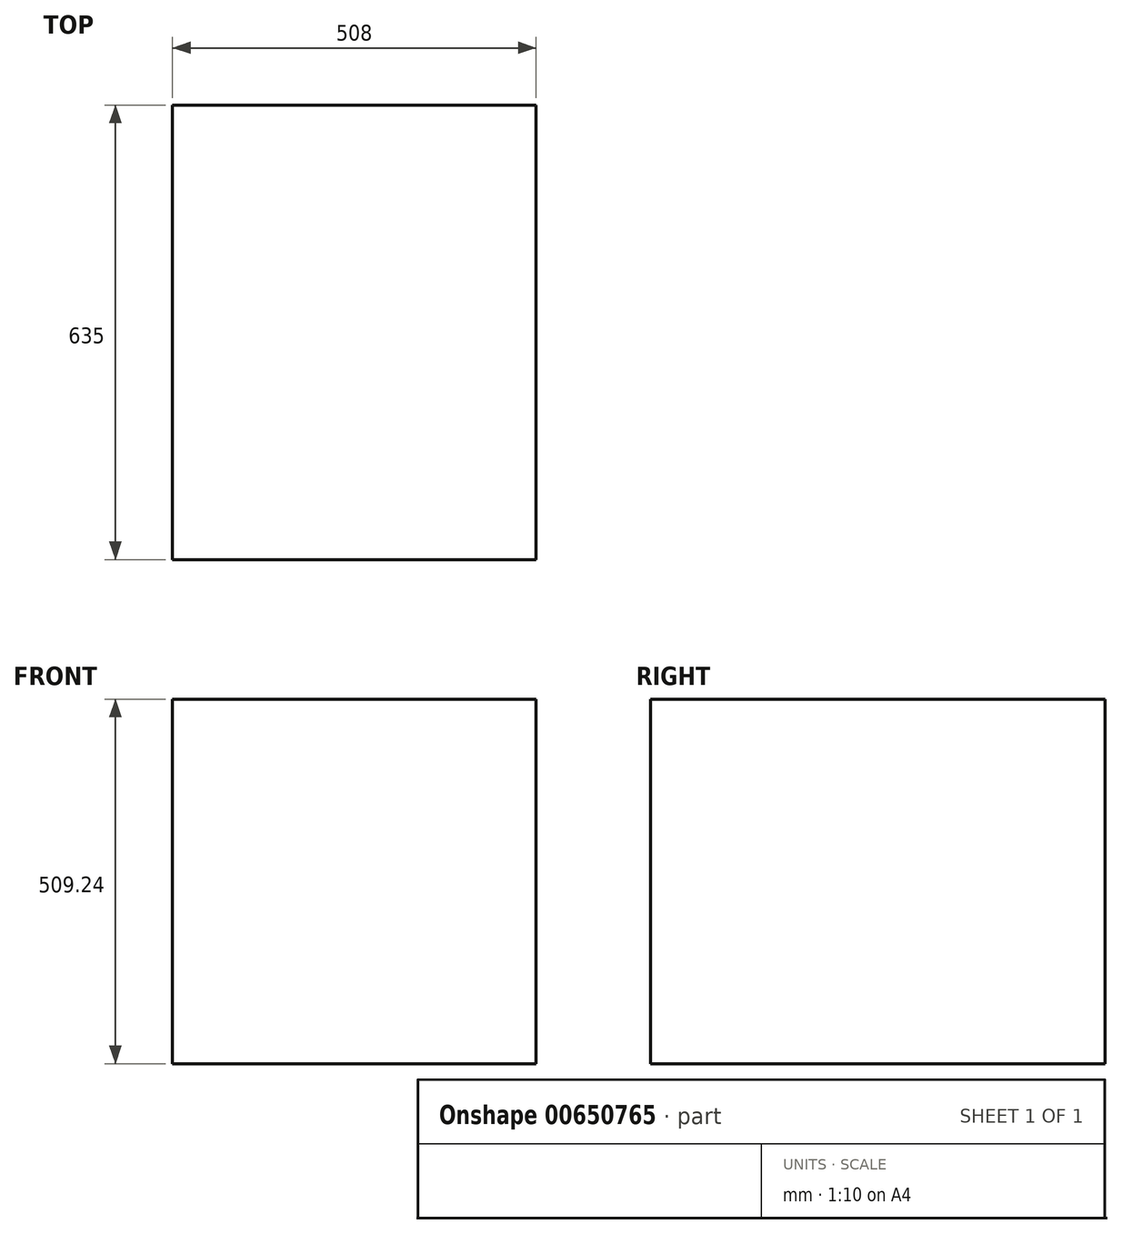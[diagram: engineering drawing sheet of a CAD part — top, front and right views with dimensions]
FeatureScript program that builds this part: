
annotation { "Feature Type Name" : "Feature", "Feature Type Description" : "" }
export const myFeature = defineFeature(function(context is Context, id is Id, definition is map)
    precondition{}
    {
        {
            var Q0;
            Q0=qCreatedBy(makeId("Front.planeOp"),FACE);
            var sketch = newSketch(context, id + "F0", { "sketchPlane" : qUnion([Q0])});
            skLineSegment(sketch, "E0.bottom", {"start": v(-252.93, 254.94) * mm, "end": v(255.07, 254.94) * mm});
            skLineSegment(sketch, "E0.top", {"start": v(-252.93, -254.3) * mm, "end": v(255.07, -254.3) * mm});
            skLineSegment(sketch, "E0.left", {"start": v(-252.93, 254.94) * mm, "end": v(-252.93, -254.3) * mm});
            skLineSegment(sketch, "E0.right", {"start": v(255.07, 254.94) * mm, "end": v(255.07, -254.3) * mm});
            skSolve(sketch);
        }
        {
            var Q0;
            Q0=makeQuery(id+"F0.imprint","IMPRINT",FACE,{"disambiguationData":[TD([[makeQuery(id+"F0.imprint","IMPRINT",EDGE,{"derivedFrom":sQuery(id+"F0.wireOp",EDGE,"E0.bottom")}),-1.0]])]});
            extrude(context, id + "F1", {"entities" : qUnion([Q0]), "oppositeDirection" : true, "depth" : 635 * mm, "offsetDistance" : 25.4 * mm});
        }
    });
